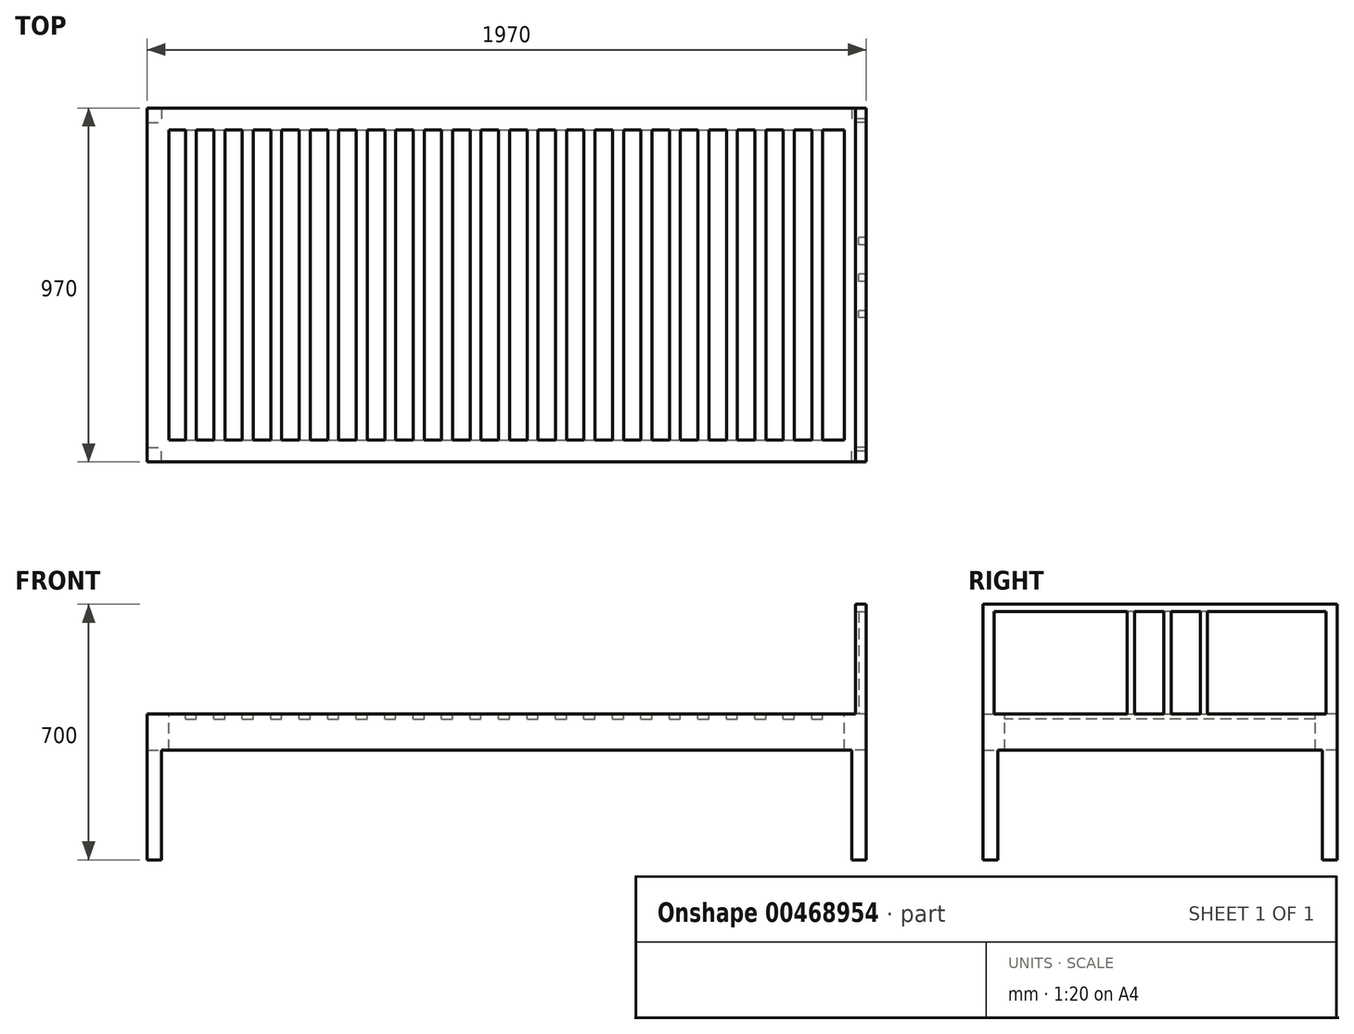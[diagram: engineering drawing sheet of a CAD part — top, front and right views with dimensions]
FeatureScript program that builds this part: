
annotation { "Feature Type Name" : "Feature", "Feature Type Description" : "" }
export const myFeature = defineFeature(function(context is Context, id is Id, definition is map)
    precondition{}
    {
        {
            var Q0;
            Q0=qCreatedBy(makeId("Top.planeOp"),FACE);
            var sketch = newSketch(context, id + "F0", { "sketchPlane" : qUnion([Q0])});
            skLineSegment(sketch, "E0.bottom", {"start": v(-985, 485) * mm, "end": v(985, 485) * mm});
            skLineSegment(sketch, "E0.top", {"start": v(-985, -485) * mm, "end": v(985, -485) * mm});
            skLineSegment(sketch, "E0.left", {"start": v(-985, 485) * mm, "end": v(-985, -485) * mm});
            skLineSegment(sketch, "E0.right", {"start": v(985, 485) * mm, "end": v(985, -485) * mm});
            skPoint(sketch, "E0.middle", {"position": v(0, 0) * mm});
            skLineSegment(sketch, "E1.bottom", {"start": v(-925, 425) * mm, "end": v(925, 425) * mm});
            skLineSegment(sketch, "E1.top", {"start": v(-925, -425) * mm, "end": v(925, -425) * mm});
            skLineSegment(sketch, "E1.left", {"start": v(-925, 425) * mm, "end": v(-925, -425) * mm});
            skLineSegment(sketch, "E1.right", {"start": v(925, 425) * mm, "end": v(925, -425) * mm});
            skLineSegment(sketch, "E2", {"start": v(-880, 425) * mm, "end": v(-880, -425) * mm});
            skLineSegment(sketch, "E3", {"start": v(-880, -425) * mm, "end": v(-850, -425) * mm});
            skLineSegment(sketch, "E4", {"start": v(-850, -425) * mm, "end": v(-850, 425) * mm});
            skLineSegment(sketch, "E5.1.0.0", {"start": v(-772, -425) * mm, "end": v(-772, 425) * mm});
            skLineSegment(sketch, "E5.1.0.1", {"start": v(-802, 425) * mm, "end": v(-802, -425) * mm});
            skLineSegment(sketch, "E5.2.0.0", {"start": v(-694, -425) * mm, "end": v(-694, 425) * mm});
            skLineSegment(sketch, "E5.2.0.1", {"start": v(-724, 425) * mm, "end": v(-724, -425) * mm});
            skLineSegment(sketch, "E5.3.0.0", {"start": v(-616, -425) * mm, "end": v(-616, 425) * mm});
            skLineSegment(sketch, "E5.3.0.1", {"start": v(-646, 425) * mm, "end": v(-646, -425) * mm});
            skLineSegment(sketch, "E5.4.0.0", {"start": v(-538, -425) * mm, "end": v(-538, 425) * mm});
            skLineSegment(sketch, "E5.4.0.1", {"start": v(-568, 425) * mm, "end": v(-568, -425) * mm});
            skLineSegment(sketch, "E5.5.0.0", {"start": v(-460, -425) * mm, "end": v(-460, 425) * mm});
            skLineSegment(sketch, "E5.5.0.1", {"start": v(-490, 425) * mm, "end": v(-490, -425) * mm});
            skLineSegment(sketch, "E5.6.0.0", {"start": v(-382, -425) * mm, "end": v(-382, 425) * mm});
            skLineSegment(sketch, "E5.6.0.1", {"start": v(-412, 425) * mm, "end": v(-412, -425) * mm});
            skLineSegment(sketch, "E5.7.0.0", {"start": v(-304, -425) * mm, "end": v(-304, 425) * mm});
            skLineSegment(sketch, "E5.7.0.1", {"start": v(-334, 425) * mm, "end": v(-334, -425) * mm});
            skLineSegment(sketch, "E5.8.0.0", {"start": v(-226, -425) * mm, "end": v(-226, 425) * mm});
            skLineSegment(sketch, "E5.8.0.1", {"start": v(-256, 425) * mm, "end": v(-256, -425) * mm});
            skLineSegment(sketch, "E5.9.0.0", {"start": v(-148, -425) * mm, "end": v(-148, 425) * mm});
            skLineSegment(sketch, "E5.9.0.1", {"start": v(-178, 425) * mm, "end": v(-178, -425) * mm});
            skLineSegment(sketch, "E5.10.0.0", {"start": v(-70, -425) * mm, "end": v(-70, 425) * mm});
            skLineSegment(sketch, "E5.10.0.1", {"start": v(-100, 425) * mm, "end": v(-100, -425) * mm});
            skLineSegment(sketch, "E5.11.0.0", {"start": v(8, -425) * mm, "end": v(8, 425) * mm});
            skLineSegment(sketch, "E5.11.0.1", {"start": v(-22, 425) * mm, "end": v(-22, -425) * mm});
            skLineSegment(sketch, "E5.12.0.0", {"start": v(86, -425) * mm, "end": v(86, 425) * mm});
            skLineSegment(sketch, "E5.12.0.1", {"start": v(56, 425) * mm, "end": v(56, -425) * mm});
            skLineSegment(sketch, "E5.13.0.0", {"start": v(164, -425) * mm, "end": v(164, 425) * mm});
            skLineSegment(sketch, "E5.13.0.1", {"start": v(134, 425) * mm, "end": v(134, -425) * mm});
            skLineSegment(sketch, "E5.14.0.0", {"start": v(242, -425) * mm, "end": v(242, 425) * mm});
            skLineSegment(sketch, "E5.14.0.1", {"start": v(212, 425) * mm, "end": v(212, -425) * mm});
            skLineSegment(sketch, "E5.15.0.0", {"start": v(320, -425) * mm, "end": v(320, 425) * mm});
            skLineSegment(sketch, "E5.15.0.1", {"start": v(290, 425) * mm, "end": v(290, -425) * mm});
            skLineSegment(sketch, "E5.16.0.0", {"start": v(398, -425) * mm, "end": v(398, 425) * mm});
            skLineSegment(sketch, "E5.16.0.1", {"start": v(368, 425) * mm, "end": v(368, -425) * mm});
            skLineSegment(sketch, "E5.17.0.0", {"start": v(476, -425) * mm, "end": v(476, 425) * mm});
            skLineSegment(sketch, "E5.17.0.1", {"start": v(446, 425) * mm, "end": v(446, -425) * mm});
            skLineSegment(sketch, "E5.18.0.0", {"start": v(554, -425) * mm, "end": v(554, 425) * mm});
            skLineSegment(sketch, "E5.18.0.1", {"start": v(524, 425) * mm, "end": v(524, -425) * mm});
            skLineSegment(sketch, "E5.19.0.0", {"start": v(632, -425) * mm, "end": v(632, 425) * mm});
            skLineSegment(sketch, "E5.19.0.1", {"start": v(602, 425) * mm, "end": v(602, -425) * mm});
            skLineSegment(sketch, "E5.20.0.0", {"start": v(710, -425) * mm, "end": v(710, 425) * mm});
            skLineSegment(sketch, "E5.20.0.1", {"start": v(680, 425) * mm, "end": v(680, -425) * mm});
            skLineSegment(sketch, "E5.21.0.0", {"start": v(788, -425) * mm, "end": v(788, 425) * mm});
            skLineSegment(sketch, "E5.21.0.1", {"start": v(758, 425) * mm, "end": v(758, -425) * mm});
            skLineSegment(sketch, "E5.22.0.0", {"start": v(866, -425) * mm, "end": v(866, 425) * mm});
            skLineSegment(sketch, "E5.22.0.1", {"start": v(836, 425) * mm, "end": v(836, -425) * mm});
            skLineSegment(sketch, "E5.direction1", {"start": v(-850, -425) * mm, "end": v(-772, -425) * mm, "construction": true});
            skSolve(sketch);
        }
        {
            var Q0;
            Q0=makeQuery(id+"F0.imprint","IMPRINT",FACE,{"disambiguationData":[TD([[makeQuery(id+"F0.imprint","IMPRINT",EDGE,{"derivedFrom":sQuery(id+"F0.wireOp",EDGE,"E0.bottom")}),-1.0]])]});
            var Q1;
            {var subQ0=sQuery(id+"F0.wireOp",EDGE,"E2");Q1=makeQuery(id+"F0.imprint","IMPRINT",FACE,{"disambiguationData":[TD([[makeQuery(id+"F0.imprint","IMPRINT",EDGE,{"derivedFrom":subQ0}),1.0]])]});}
            var Q2;
            {var subQ0=sQuery(id+"F0.wireOp",EDGE,"E5.1.0.0");Q2=makeQuery(id+"F0.imprint","IMPRINT",FACE,{"disambiguationData":[TD([[makeQuery(id+"F0.imprint","IMPRINT",EDGE,{"derivedFrom":subQ0}),1.0]])]});}
            var Q3;
            {var subQ0=sQuery(id+"F0.wireOp",EDGE,"E5.2.0.0");Q3=makeQuery(id+"F0.imprint","IMPRINT",FACE,{"disambiguationData":[TD([[makeQuery(id+"F0.imprint","IMPRINT",EDGE,{"derivedFrom":subQ0}),1.0]])]});}
            var Q4;
            {var subQ0=sQuery(id+"F0.wireOp",EDGE,"E5.3.0.0");Q4=makeQuery(id+"F0.imprint","IMPRINT",FACE,{"disambiguationData":[TD([[makeQuery(id+"F0.imprint","IMPRINT",EDGE,{"derivedFrom":subQ0}),1.0]])]});}
            var Q5;
            {var subQ0=sQuery(id+"F0.wireOp",EDGE,"E5.4.0.0");Q5=makeQuery(id+"F0.imprint","IMPRINT",FACE,{"disambiguationData":[TD([[makeQuery(id+"F0.imprint","IMPRINT",EDGE,{"derivedFrom":subQ0}),1.0]])]});}
            var Q6;
            {var subQ0=sQuery(id+"F0.wireOp",EDGE,"E5.5.0.0");Q6=makeQuery(id+"F0.imprint","IMPRINT",FACE,{"disambiguationData":[TD([[makeQuery(id+"F0.imprint","IMPRINT",EDGE,{"derivedFrom":subQ0}),1.0]])]});}
            var Q7;
            {var subQ0=sQuery(id+"F0.wireOp",EDGE,"E5.6.0.0");Q7=makeQuery(id+"F0.imprint","IMPRINT",FACE,{"disambiguationData":[TD([[makeQuery(id+"F0.imprint","IMPRINT",EDGE,{"derivedFrom":subQ0}),1.0]])]});}
            var Q8;
            {var subQ0=sQuery(id+"F0.wireOp",EDGE,"E5.7.0.0");Q8=makeQuery(id+"F0.imprint","IMPRINT",FACE,{"disambiguationData":[TD([[makeQuery(id+"F0.imprint","IMPRINT",EDGE,{"derivedFrom":subQ0}),1.0]])]});}
            var Q9;
            {var subQ0=sQuery(id+"F0.wireOp",EDGE,"E5.8.0.0");Q9=makeQuery(id+"F0.imprint","IMPRINT",FACE,{"disambiguationData":[TD([[makeQuery(id+"F0.imprint","IMPRINT",EDGE,{"derivedFrom":subQ0}),1.0]])]});}
            var Q10;
            {var subQ0=sQuery(id+"F0.wireOp",EDGE,"E5.9.0.0");Q10=makeQuery(id+"F0.imprint","IMPRINT",FACE,{"disambiguationData":[TD([[makeQuery(id+"F0.imprint","IMPRINT",EDGE,{"derivedFrom":subQ0}),1.0]])]});}
            var Q11;
            {var subQ0=sQuery(id+"F0.wireOp",EDGE,"E5.10.0.0");Q11=makeQuery(id+"F0.imprint","IMPRINT",FACE,{"disambiguationData":[TD([[makeQuery(id+"F0.imprint","IMPRINT",EDGE,{"derivedFrom":subQ0}),1.0]])]});}
            var Q12;
            {var subQ0=sQuery(id+"F0.wireOp",EDGE,"E5.11.0.0");Q12=makeQuery(id+"F0.imprint","IMPRINT",FACE,{"disambiguationData":[TD([[makeQuery(id+"F0.imprint","IMPRINT",EDGE,{"derivedFrom":subQ0}),1.0]])]});}
            var Q13;
            {var subQ0=sQuery(id+"F0.wireOp",EDGE,"E5.12.0.0");Q13=makeQuery(id+"F0.imprint","IMPRINT",FACE,{"disambiguationData":[TD([[makeQuery(id+"F0.imprint","IMPRINT",EDGE,{"derivedFrom":subQ0}),1.0]])]});}
            var Q14;
            {var subQ0=sQuery(id+"F0.wireOp",EDGE,"E5.13.0.0");Q14=makeQuery(id+"F0.imprint","IMPRINT",FACE,{"disambiguationData":[TD([[makeQuery(id+"F0.imprint","IMPRINT",EDGE,{"derivedFrom":subQ0}),1.0]])]});}
            var Q15;
            {var subQ0=sQuery(id+"F0.wireOp",EDGE,"E5.14.0.0");Q15=makeQuery(id+"F0.imprint","IMPRINT",FACE,{"disambiguationData":[TD([[makeQuery(id+"F0.imprint","IMPRINT",EDGE,{"derivedFrom":subQ0}),1.0]])]});}
            var Q16;
            {var subQ0=sQuery(id+"F0.wireOp",EDGE,"E5.15.0.0");Q16=makeQuery(id+"F0.imprint","IMPRINT",FACE,{"disambiguationData":[TD([[makeQuery(id+"F0.imprint","IMPRINT",EDGE,{"derivedFrom":subQ0}),1.0]])]});}
            var Q17;
            {var subQ0=sQuery(id+"F0.wireOp",EDGE,"E5.16.0.0");Q17=makeQuery(id+"F0.imprint","IMPRINT",FACE,{"disambiguationData":[TD([[makeQuery(id+"F0.imprint","IMPRINT",EDGE,{"derivedFrom":subQ0}),1.0]])]});}
            var Q18;
            {var subQ0=sQuery(id+"F0.wireOp",EDGE,"E5.17.0.0");Q18=makeQuery(id+"F0.imprint","IMPRINT",FACE,{"disambiguationData":[TD([[makeQuery(id+"F0.imprint","IMPRINT",EDGE,{"derivedFrom":subQ0}),1.0]])]});}
            var Q19;
            {var subQ0=sQuery(id+"F0.wireOp",EDGE,"E5.18.0.0");Q19=makeQuery(id+"F0.imprint","IMPRINT",FACE,{"disambiguationData":[TD([[makeQuery(id+"F0.imprint","IMPRINT",EDGE,{"derivedFrom":subQ0}),1.0]])]});}
            var Q20;
            {var subQ0=sQuery(id+"F0.wireOp",EDGE,"E5.19.0.0");Q20=makeQuery(id+"F0.imprint","IMPRINT",FACE,{"disambiguationData":[TD([[makeQuery(id+"F0.imprint","IMPRINT",EDGE,{"derivedFrom":subQ0}),1.0]])]});}
            var Q21;
            {var subQ0=sQuery(id+"F0.wireOp",EDGE,"E5.20.0.0");Q21=makeQuery(id+"F0.imprint","IMPRINT",FACE,{"disambiguationData":[TD([[makeQuery(id+"F0.imprint","IMPRINT",EDGE,{"derivedFrom":subQ0}),1.0]])]});}
            var Q22;
            {var subQ0=sQuery(id+"F0.wireOp",EDGE,"E5.21.0.0");Q22=makeQuery(id+"F0.imprint","IMPRINT",FACE,{"disambiguationData":[TD([[makeQuery(id+"F0.imprint","IMPRINT",EDGE,{"derivedFrom":subQ0}),1.0]])]});}
            var Q23;
            {var subQ0=sQuery(id+"F0.wireOp",EDGE,"E5.22.0.0");Q23=makeQuery(id+"F0.imprint","IMPRINT",FACE,{"disambiguationData":[TD([[makeQuery(id+"F0.imprint","IMPRINT",EDGE,{"derivedFrom":subQ0}),1.0]])]});}
            extrude(context, id + "F1", {"entities" : qUnion([Q0, Q1, Q2, Q3, Q4, Q5, Q6, Q7, Q8, Q9, Q10, Q11, Q12, Q13, Q14, Q15, Q16, Q17, Q18, Q19, Q20, Q21, Q22, Q23]), "oppositeDirection" : true, "depth" : 15 * mm});
        }
        {
            var Q0;
            Q0 = qSketchRegion(id + "F0", true);
            extrude(context, id + "F2", {"entities" : qUnion([Q0]), "operationType" : NewBodyOperationType.ADD, "oppositeDirection" : true, "depth" : 100 * mm});
        }
        {
            var Q0;
            Q0=makeQuery(id+"F1.opExtrude","CAP_FACE",FACE,{"disambiguationData":[OSD([sQuery(id+"F0.wireOp",EDGE,"E0.bottom"),sQuery(id+"F0.wireOp",EDGE,"E0.top"),sQuery(id+"F0.wireOp",EDGE,"E0.left"),sQuery(id+"F0.wireOp",EDGE,"E0.right"),sQuery(id+"F0.wireOp",EDGE,"E1.bottom"),sQuery(id+"F0.wireOp",EDGE,"E1.top"),sQuery(id+"F0.wireOp",EDGE,"E1.left"),sQuery(id+"F0.wireOp",EDGE,"E1.right"),sQuery(id+"F0.wireOp",EDGE,"E2"),sQuery(id+"F0.wireOp",EDGE,"E4"),sQuery(id+"F0.wireOp",EDGE,"E5.1.0.0"),sQuery(id+"F0.wireOp",EDGE,"E5.1.0.1"),sQuery(id+"F0.wireOp",EDGE,"E5.2.0.0"),sQuery(id+"F0.wireOp",EDGE,"E5.2.0.1"),sQuery(id+"F0.wireOp",EDGE,"E5.3.0.0"),sQuery(id+"F0.wireOp",EDGE,"E5.3.0.1"),sQuery(id+"F0.wireOp",EDGE,"E5.4.0.0"),sQuery(id+"F0.wireOp",EDGE,"E5.4.0.1"),sQuery(id+"F0.wireOp",EDGE,"E5.5.0.0"),sQuery(id+"F0.wireOp",EDGE,"E5.5.0.1"),sQuery(id+"F0.wireOp",EDGE,"E5.6.0.0"),sQuery(id+"F0.wireOp",EDGE,"E5.6.0.1"),sQuery(id+"F0.wireOp",EDGE,"E5.7.0.0"),sQuery(id+"F0.wireOp",EDGE,"E5.7.0.1"),sQuery(id+"F0.wireOp",EDGE,"E5.8.0.0"),sQuery(id+"F0.wireOp",EDGE,"E5.8.0.1"),sQuery(id+"F0.wireOp",EDGE,"E5.9.0.0"),sQuery(id+"F0.wireOp",EDGE,"E5.9.0.1"),sQuery(id+"F0.wireOp",EDGE,"E5.10.0.0"),sQuery(id+"F0.wireOp",EDGE,"E5.10.0.1"),sQuery(id+"F0.wireOp",EDGE,"E5.11.0.0"),sQuery(id+"F0.wireOp",EDGE,"E5.11.0.1"),sQuery(id+"F0.wireOp",EDGE,"E5.12.0.0"),sQuery(id+"F0.wireOp",EDGE,"E5.12.0.1"),sQuery(id+"F0.wireOp",EDGE,"E5.13.0.0"),sQuery(id+"F0.wireOp",EDGE,"E5.13.0.1"),sQuery(id+"F0.wireOp",EDGE,"E5.14.0.0"),sQuery(id+"F0.wireOp",EDGE,"E5.14.0.1"),sQuery(id+"F0.wireOp",EDGE,"E5.15.0.0"),sQuery(id+"F0.wireOp",EDGE,"E5.15.0.1"),sQuery(id+"F0.wireOp",EDGE,"E5.16.0.0"),sQuery(id+"F0.wireOp",EDGE,"E5.16.0.1"),sQuery(id+"F0.wireOp",EDGE,"E5.17.0.0"),sQuery(id+"F0.wireOp",EDGE,"E5.17.0.1"),sQuery(id+"F0.wireOp",EDGE,"E5.18.0.0"),sQuery(id+"F0.wireOp",EDGE,"E5.18.0.1"),sQuery(id+"F0.wireOp",EDGE,"E5.19.0.0"),sQuery(id+"F0.wireOp",EDGE,"E5.19.0.1"),sQuery(id+"F0.wireOp",EDGE,"E5.20.0.0"),sQuery(id+"F0.wireOp",EDGE,"E5.20.0.1"),sQuery(id+"F0.wireOp",EDGE,"E5.21.0.0"),sQuery(id+"F0.wireOp",EDGE,"E5.21.0.1"),sQuery(id+"F0.wireOp",EDGE,"E5.22.0.0"),sQuery(id+"F0.wireOp",EDGE,"E5.22.0.1")])],"isStart":true});
            var sketch = newSketch(context, id + "F3", { "sketchPlane" : qUnion([Q0])});
            skLineSegment(sketch, "E6.bottom", {"start": v(985, 485) * mm, "end": v(955, 485) * mm});
            skLineSegment(sketch, "E6.top", {"start": v(985, 455) * mm, "end": v(955, 455) * mm});
            skLineSegment(sketch, "E6.left", {"start": v(985, 485) * mm, "end": v(985, 455) * mm});
            skLineSegment(sketch, "E6.right", {"start": v(955, 485) * mm, "end": v(955, 455) * mm});
            skLineSegment(sketch, "E7.bottom", {"start": v(985, -485) * mm, "end": v(955, -485) * mm});
            skLineSegment(sketch, "E7.top", {"start": v(985, -455) * mm, "end": v(955, -455) * mm});
            skLineSegment(sketch, "E7.left", {"start": v(985, -485) * mm, "end": v(985, -455) * mm});
            skLineSegment(sketch, "E7.right", {"start": v(955, -485) * mm, "end": v(955, -455) * mm});
            skLineSegment(sketch, "E8.bottom", {"start": v(985, -90) * mm, "end": v(965, -90) * mm});
            skLineSegment(sketch, "E8.top", {"start": v(985, -70) * mm, "end": v(965, -70) * mm});
            skLineSegment(sketch, "E8.left", {"start": v(985, -90) * mm, "end": v(985, -70) * mm});
            skLineSegment(sketch, "E8.right", {"start": v(965, -90) * mm, "end": v(965, -70) * mm});
            skLineSegment(sketch, "E9.bottom", {"start": v(985, 10) * mm, "end": v(965, 10) * mm});
            skLineSegment(sketch, "E9.top", {"start": v(985, 30) * mm, "end": v(965, 30) * mm});
            skLineSegment(sketch, "E9.left", {"start": v(985, 10) * mm, "end": v(985, 30) * mm});
            skLineSegment(sketch, "E9.right", {"start": v(965, 10) * mm, "end": v(965, 30) * mm});
            skLineSegment(sketch, "E10.bottom", {"start": v(985, 110) * mm, "end": v(965, 110) * mm});
            skLineSegment(sketch, "E10.top", {"start": v(985, 130) * mm, "end": v(965, 130) * mm});
            skLineSegment(sketch, "E10.left", {"start": v(985, 110) * mm, "end": v(985, 130) * mm});
            skLineSegment(sketch, "E10.right", {"start": v(965, 110) * mm, "end": v(965, 130) * mm});
            skSolve(sketch);
        }
        {
            var Q0;
            Q0 = qSketchRegion(id + "F3", true);
            extrude(context, id + "F4", {"entities" : qUnion([Q0]), "operationType" : NewBodyOperationType.ADD, "depth" : 300 * mm});
        }
        {
            var Q0;
            {var subQ0=sQuery(id+"F0.wireOp",EDGE,"E0.top");Q0=makeQuery(id+"F4.boolean.opBoolean","MERGE",FACE,{"derivedFrom":[makeQuery(id+"F2.boolean.opBoolean","MERGE",FACE,{"derivedFrom":[makeQuery(id+"F1.opExtrude","SWEPT_FACE",FACE,{"disambiguationData":[OSD([subQ0])]}),makeQuery(id+"F2.opExtrude","SWEPT_FACE",FACE,{"disambiguationData":[OSD([subQ0])]})]}),makeQuery(id+"F4.opExtrude","SWEPT_FACE",FACE,{"disambiguationData":[OSD([sQuery(id+"F3.wireOp",EDGE,"E7.bottom")])]})]});}
            var sketch = newSketch(context, id + "F5", { "sketchPlane" : qUnion([Q0])});
            skLineSegment(sketch, "E11.bottom", {"start": v(955, 300) * mm, "end": v(985, 300) * mm});
            skLineSegment(sketch, "E11.top", {"start": v(955, 280) * mm, "end": v(985, 280) * mm});
            skLineSegment(sketch, "E11.left", {"start": v(955, 300) * mm, "end": v(955, 280) * mm});
            skLineSegment(sketch, "E11.right", {"start": v(985, 300) * mm, "end": v(985, 280) * mm});
            skSolve(sketch);
        }
        {
            var Q0;
            Q0 = qSketchRegion(id + "F5", true);
            var Q1;
            {var subQ0=sQuery(id+"F0.wireOp",EDGE,"E0.bottom");Q1=makeQuery(id+"F4.boolean.opBoolean","MERGE",FACE,{"derivedFrom":[makeQuery(id+"F2.boolean.opBoolean","MERGE",FACE,{"derivedFrom":[makeQuery(id+"F1.opExtrude","SWEPT_FACE",FACE,{"disambiguationData":[OSD([subQ0])]}),makeQuery(id+"F2.opExtrude","SWEPT_FACE",FACE,{"disambiguationData":[OSD([subQ0])]})]}),makeQuery(id+"F4.opExtrude","SWEPT_FACE",FACE,{"disambiguationData":[OSD([sQuery(id+"F3.wireOp",EDGE,"E6.bottom")])]})]});}
            extrude(context, id + "F6", {"entities" : qUnion([Q0]), "operationType" : NewBodyOperationType.ADD, "endBound" : BoundingType.UP_TO_SURFACE, "oppositeDirection" : true, "endBoundEntityFace" : qUnion([Q1]), "depth" : 25 * mm});
        }
        {
            var Q0;
            Q0=makeQuery(id+"F2.opExtrude","CAP_FACE",FACE,{"disambiguationData":[OSD([sQuery(id+"F0.wireOp",EDGE,"E0.bottom"),sQuery(id+"F0.wireOp",EDGE,"E0.top"),sQuery(id+"F0.wireOp",EDGE,"E0.left"),sQuery(id+"F0.wireOp",EDGE,"E0.right"),sQuery(id+"F0.wireOp",EDGE,"E1.bottom"),sQuery(id+"F0.wireOp",EDGE,"E1.top"),sQuery(id+"F0.wireOp",EDGE,"E1.left"),sQuery(id+"F0.wireOp",EDGE,"E1.right"),sQuery(id+"F0.wireOp",EDGE,"E3")])],"isStart":false});
            var sketch = newSketch(context, id + "F7", { "sketchPlane" : qUnion([Q0])});
            skLineSegment(sketch, "E12.bottom", {"start": v(985, 485) * mm, "end": v(945, 485) * mm});
            skLineSegment(sketch, "E12.top", {"start": v(985, 445) * mm, "end": v(945, 445) * mm});
            skLineSegment(sketch, "E12.left", {"start": v(985, 485) * mm, "end": v(985, 445) * mm});
            skLineSegment(sketch, "E12.right", {"start": v(945, 485) * mm, "end": v(945, 445) * mm});
            skLineSegment(sketch, "E13.bottom", {"start": v(-985, 485) * mm, "end": v(-945, 485) * mm});
            skLineSegment(sketch, "E13.top", {"start": v(-985, 445) * mm, "end": v(-945, 445) * mm});
            skLineSegment(sketch, "E13.left", {"start": v(-985, 485) * mm, "end": v(-985, 445) * mm});
            skLineSegment(sketch, "E13.right", {"start": v(-945, 485) * mm, "end": v(-945, 445) * mm});
            skLineSegment(sketch, "E14.bottom", {"start": v(-985, -485) * mm, "end": v(-945, -485) * mm});
            skLineSegment(sketch, "E14.top", {"start": v(-985, -445) * mm, "end": v(-945, -445) * mm});
            skLineSegment(sketch, "E14.left", {"start": v(-985, -485) * mm, "end": v(-985, -445) * mm});
            skLineSegment(sketch, "E14.right", {"start": v(-945, -485) * mm, "end": v(-945, -445) * mm});
            skLineSegment(sketch, "E15.bottom", {"start": v(985, -485) * mm, "end": v(945, -485) * mm});
            skLineSegment(sketch, "E15.top", {"start": v(985, -445) * mm, "end": v(945, -445) * mm});
            skLineSegment(sketch, "E15.left", {"start": v(985, -485) * mm, "end": v(985, -445) * mm});
            skLineSegment(sketch, "E15.right", {"start": v(945, -485) * mm, "end": v(945, -445) * mm});
            skSolve(sketch);
        }
        {
            var Q0;
            Q0 = qSketchRegion(id + "F7", true);
            extrude(context, id + "F8", {"entities" : qUnion([Q0]), "operationType" : NewBodyOperationType.ADD, "depth" : 300 * mm});
        }
    });
